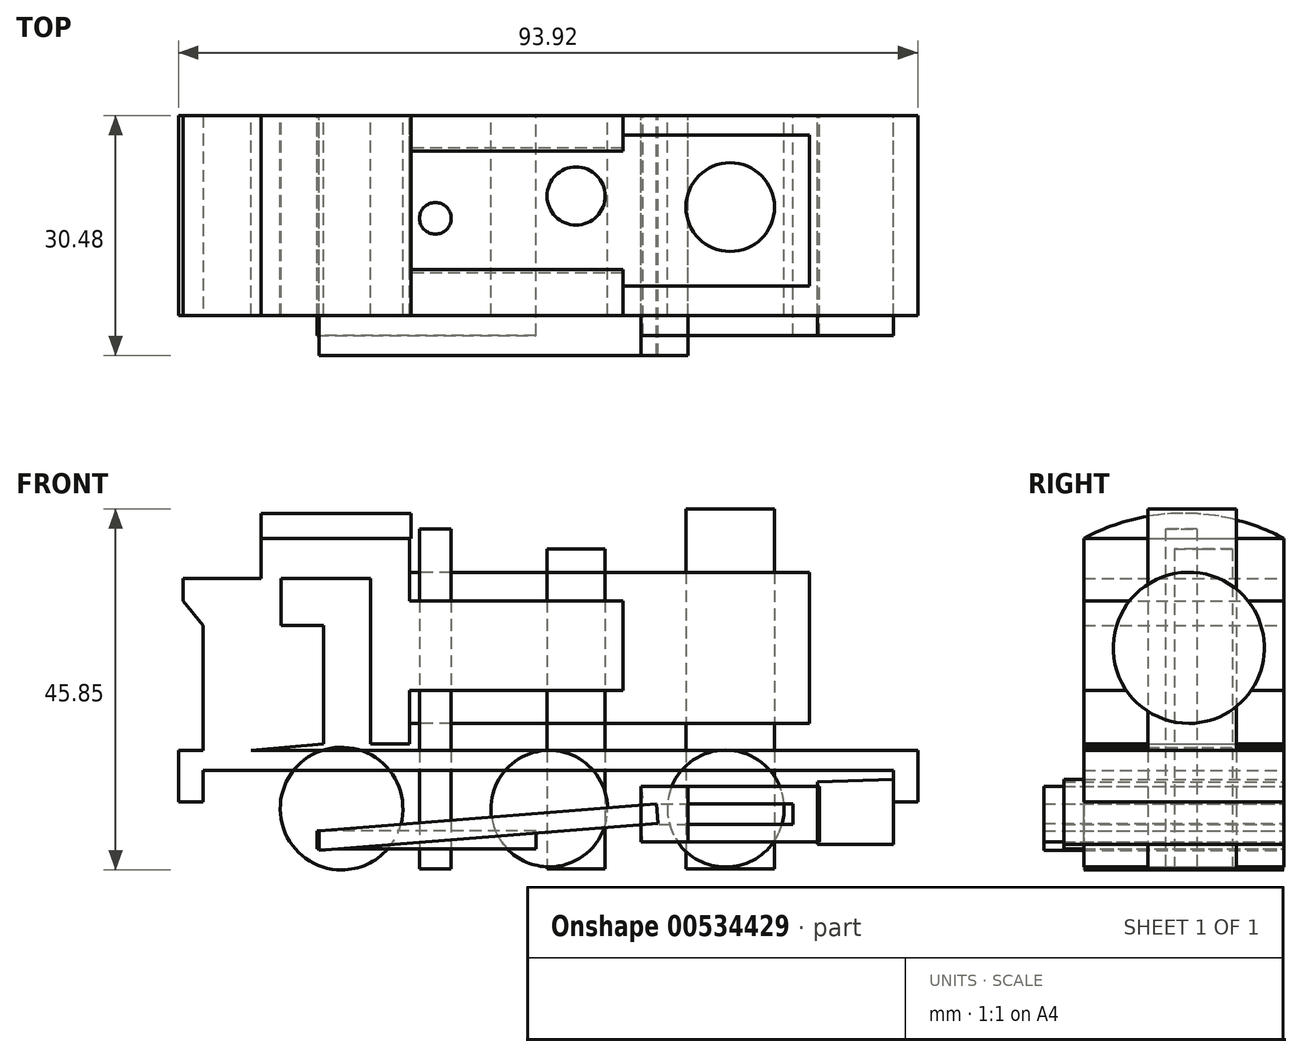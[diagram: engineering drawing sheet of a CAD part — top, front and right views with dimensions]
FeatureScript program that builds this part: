
annotation { "Feature Type Name" : "Feature", "Feature Type Description" : "" }
export const myFeature = defineFeature(function(context is Context, id is Id, definition is map)
    precondition{}
    {
        {
            var Q0;
            Q0=qCreatedBy(makeId("Front.planeOp"),FACE);
            var sketch = newSketch(context, id + "F0", { "sketchPlane" : qUnion([Q0])});
            skCircle(sketch, "E0", {"center": v(-8.65, 7.66) * mm, "radius": 7.8 * mm});
            skCircle(sketch, "E1", {"center": v(17.73, 7.66) * mm, "radius": 7.4 * mm});
            skCircle(sketch, "E2", {"center": v(40.15, 7.66) * mm, "radius": 7.43 * mm});
            skSolve(sketch);
        }
        {
            var Q0;
            Q0=makeQuery(id+"F0.imprint","IMPRINT",FACE,{"disambiguationData":[TD([[makeQuery(id+"F0.imprint","IMPRINT",EDGE,{"derivedFrom":sQuery(id+"F0.wireOp",EDGE,"E0")}),1.0]])]});
            var Q1;
            Q1=makeQuery(id+"F0.imprint","IMPRINT",FACE,{"disambiguationData":[TD([[makeQuery(id+"F0.imprint","IMPRINT",EDGE,{"derivedFrom":sQuery(id+"F0.wireOp",EDGE,"E1")}),1.0]])]});
            var Q2;
            Q2=makeQuery(id+"F0.imprint","IMPRINT",FACE,{"disambiguationData":[TD([[makeQuery(id+"F0.imprint","IMPRINT",EDGE,{"derivedFrom":sQuery(id+"F0.wireOp",EDGE,"E2")}),1.0]])]});
            extrude(context, id + "F1", {"entities" : qUnion([Q0, Q1, Q2]), "depth" : 25.4 * mm, "offsetDistance" : 25.4 * mm});
        }
        {
            var Q0;
            Q0=qCreatedBy(makeId("Front.planeOp"),FACE);
            var sketch = newSketch(context, id + "F2", { "sketchPlane" : qUnion([Q0])});
            skLineSegment(sketch, "E3", {"start": v(-12.06, 15.04) * mm, "end": v(64.55, 15.04) * mm});
            skLineSegment(sketch, "E4", {"start": v(64.55, 15.04) * mm, "end": v(64.55, 8.51) * mm});
            skLineSegment(sketch, "E5", {"start": v(64.55, 8.51) * mm, "end": v(61.43, 8.51) * mm});
            skLineSegment(sketch, "E6", {"start": v(61.43, 8.51) * mm, "end": v(61.43, 12.48) * mm});
            skLineSegment(sketch, "E7", {"start": v(61.43, 12.48) * mm, "end": v(-26.24, 12.48) * mm});
            skLineSegment(sketch, "E8", {"start": v(-26.24, 12.48) * mm, "end": v(-26.24, 8.51) * mm});
            skLineSegment(sketch, "E9", {"start": v(-26.24, 8.51) * mm, "end": v(-29.37, 8.51) * mm});
            skLineSegment(sketch, "E10", {"start": v(-29.37, 8.51) * mm, "end": v(-29.37, 15.04) * mm});
            skLineSegment(sketch, "E11", {"start": v(-29.37, 15.04) * mm, "end": v(-12.06, 15.04) * mm});
            skSolve(sketch);
        }
        {
            var Q0;
            Q0=makeQuery(id+"F2.imprint","IMPRINT",FACE,{"disambiguationData":[TD([[makeQuery(id+"F2.imprint","IMPRINT",EDGE,{"derivedFrom":sQuery(id+"F2.wireOp",EDGE,"E3")}),-1.0]])]});
            extrude(context, id + "F3", {"entities" : qUnion([Q0]), "depth" : 25.4 * mm, "offsetDistance" : 25.4 * mm});
        }
        {
            var Q0;
            Q0=qCreatedBy(makeId("Front.planeOp"),FACE);
            var sketch = newSketch(context, id + "F4", { "sketchPlane" : qUnion([Q0])});
            skLineSegment(sketch, "E12", {"start": v(-26.24, 14.47) * mm, "end": v(-26.24, 30.93) * mm});
            skLineSegment(sketch, "E13", {"start": v(-26.24, 30.93) * mm, "end": v(-28.8, 34.05) * mm});
            skLineSegment(sketch, "E14", {"start": v(-28.8, 34.05) * mm, "end": v(-28.8, 36.88) * mm});
            skLineSegment(sketch, "E15", {"start": v(-28.8, 36.88) * mm, "end": v(-18.87, 36.88) * mm});
            skLineSegment(sketch, "E16", {"start": v(-18.87, 36.88) * mm, "end": v(-18.87, 42) * mm});
            skLineSegment(sketch, "E17", {"start": v(-18.87, 42) * mm, "end": v(0, 42) * mm});
            skLineSegment(sketch, "E18", {"start": v(0, 42) * mm, "end": v(0, 34.05) * mm});
            skLineSegment(sketch, "E19", {"start": v(0, 34.05) * mm, "end": v(27.1, 34.05) * mm});
            skLineSegment(sketch, "E20", {"start": v(27.1, 34.05) * mm, "end": v(27.1, 22.7) * mm});
            skLineSegment(sketch, "E21", {"start": v(27.1, 22.7) * mm, "end": v(0, 22.7) * mm});
            skLineSegment(sketch, "E22", {"start": v(0, 22.7) * mm, "end": v(0, 15.89) * mm});
            skLineSegment(sketch, "E23", {"start": v(0, 15.89) * mm, "end": v(-4.97, 15.89) * mm});
            skLineSegment(sketch, "E24", {"start": v(-4.97, 15.89) * mm, "end": v(-4.97, 36.88) * mm});
            skLineSegment(sketch, "E25", {"start": v(-4.97, 36.88) * mm, "end": v(-16.31, 36.88) * mm});
            skLineSegment(sketch, "E26", {"start": v(-16.31, 36.88) * mm, "end": v(-16.31, 30.93) * mm});
            skLineSegment(sketch, "E27", {"start": v(-16.31, 30.93) * mm, "end": v(-10.92, 30.93) * mm});
            skLineSegment(sketch, "E28", {"start": v(-10.92, 30.93) * mm, "end": v(-10.92, 15.89) * mm});
            skLineSegment(sketch, "E29", {"start": v(-10.92, 15.89) * mm, "end": v(-26.24, 14.47) * mm});
            skSolve(sketch);
        }
        {
            var Q0;
            Q0=makeQuery(id+"F4.imprint","IMPRINT",FACE,{"disambiguationData":[TD([[makeQuery(id+"F4.imprint","IMPRINT",EDGE,{"derivedFrom":sQuery(id+"F4.wireOp",EDGE,"E12")}),-1.0]])]});
            extrude(context, id + "F5", {"entities" : qUnion([Q0]), "operationType" : NewBodyOperationType.ADD, "depth" : 25.4 * mm, "offsetDistance" : 25.4 * mm});
        }
        {
            var Q0;
            Q0=qCreatedBy(makeId("Right.planeOp"),FACE);
            var sketch = newSketch(context, id + "F6", { "sketchPlane" : qUnion([Q0])});
            skCircle(sketch, "E30", {"center": v(-12.06, 28.09) * mm, "radius": 9.6 * mm});
            skSolve(sketch);
        }
        {
            var Q0;
            Q0=makeQuery(id+"F6.imprint","IMPRINT",FACE,{"disambiguationData":[TD([[makeQuery(id+"F6.imprint","IMPRINT",EDGE,{"derivedFrom":sQuery(id+"F6.wireOp",EDGE,"E30")}),1.0]])]});
            var Q1;
            Q1=sQuery(id+"F6.wireOp",EDGE,"E30");
            extrude(context, id + "F7", {"entities" : qUnion([Q0]), "operationType" : NewBodyOperationType.ADD, "surfaceEntities" : qUnion([Q1]), "depth" : 50.8 * mm, "offsetDistance" : 25.4 * mm});
        }
        {
            var Q0;
            Q0=qCreatedBy(makeId("Front.planeOp"),FACE);
            var sketch = newSketch(context, id + "F8", { "sketchPlane" : qUnion([Q0])});
            skLineSegment(sketch, "E31", {"start": v(61.43, 11.35) * mm, "end": v(61.43, 3.12) * mm});
            skLineSegment(sketch, "E32", {"start": v(61.43, 3.12) * mm, "end": v(51.78, 3.12) * mm});
            skLineSegment(sketch, "E33", {"start": v(51.78, 3.12) * mm, "end": v(51.78, 11.07) * mm});
            skLineSegment(sketch, "E34", {"start": v(51.78, 11.07) * mm, "end": v(61.43, 11.35) * mm});
            skSolve(sketch);
        }
        {
            var Q0;
            Q0=makeQuery(id+"F8.imprint","IMPRINT",FACE,{"disambiguationData":[TD([[makeQuery(id+"F8.imprint","IMPRINT",EDGE,{"derivedFrom":sQuery(id+"F8.wireOp",EDGE,"E31")}),-1.0]])]});
            extrude(context, id + "F9", {"entities" : qUnion([Q0]), "operationType" : NewBodyOperationType.ADD, "depth" : 27.94 * mm, "offsetDistance" : 25.4 * mm});
        }
        {
            var Q0;
            Q0=qCreatedBy(makeId("Front.planeOp"),FACE);
            var sketch = newSketch(context, id + "F10", { "sketchPlane" : qUnion([Q0])});
            skLineSegment(sketch, "E35", {"start": v(52.06, 10.5) * mm, "end": v(29.37, 10.5) * mm});
            skLineSegment(sketch, "E36", {"start": v(52.06, 3.4) * mm, "end": v(29.65, 3.4) * mm});
            skLineSegment(sketch, "E37", {"start": v(29.65, 3.4) * mm, "end": v(29.37, 5.67) * mm});
            skLineSegment(sketch, "E38", {"start": v(29.37, 5.67) * mm, "end": v(48.66, 5.67) * mm});
            skLineSegment(sketch, "E39", {"start": v(29.37, 10.5) * mm, "end": v(29.65, 8.23) * mm});
            skLineSegment(sketch, "E40", {"start": v(29.65, 8.23) * mm, "end": v(48.66, 8.23) * mm});
            skLineSegment(sketch, "E41", {"start": v(48.66, 8.23) * mm, "end": v(48.66, 5.67) * mm});
            skLineSegment(sketch, "E42", {"start": v(52.06, 10.5) * mm, "end": v(52.06, 3.4) * mm});
            skLineSegment(sketch, "E43", {"start": v(52.06, 3.4) * mm, "end": v(52.06, 10.5) * mm});
            skSolve(sketch);
        }
        {
            var Q0;
            Q0=makeQuery(id+"F10.imprint","IMPRINT",FACE,{"disambiguationData":[TD([[makeQuery(id+"F10.imprint","IMPRINT",EDGE,{"derivedFrom":sQuery(id+"F10.wireOp",EDGE,"E35")}),1.0]])]});
            extrude(context, id + "F11", {"entities" : qUnion([Q0]), "depth" : 27.94 * mm, "offsetDistance" : 25.4 * mm});
        }
        {
            var Q0;
            Q0=qCreatedBy(makeId("Front.planeOp"),FACE);
            var sketch = newSketch(context, id + "F12", { "sketchPlane" : qUnion([Q0])});
            skLineSegment(sketch, "E44", {"start": v(-11.77, 4.82) * mm, "end": v(-11.77, 2.55) * mm});
            skLineSegment(sketch, "E45", {"start": v(-11.77, 2.55) * mm, "end": v(16.03, 2.55) * mm});
            skLineSegment(sketch, "E46", {"start": v(16.03, 2.55) * mm, "end": v(16.03, 4.82) * mm});
            skLineSegment(sketch, "E47", {"start": v(16.03, 4.82) * mm, "end": v(-11.77, 4.82) * mm});
            skSolve(sketch);
        }
        {
            var Q0;
            Q0=makeQuery(id+"F12.imprint","IMPRINT",FACE,{"disambiguationData":[TD([[makeQuery(id+"F12.imprint","IMPRINT",EDGE,{"derivedFrom":sQuery(id+"F12.wireOp",EDGE,"E44")}),1.0]])]});
            extrude(context, id + "F13", {"entities" : qUnion([Q0]), "depth" : 27.94 * mm, "offsetDistance" : 25.4 * mm});
        }
        {
            var Q0;
            Q0=qCreatedBy(makeId("Front.planeOp"),FACE);
            var sketch = newSketch(context, id + "F14", { "sketchPlane" : qUnion([Q0])});
            skLineSegment(sketch, "E48", {"start": v(29.37, 10.5) * mm, "end": v(35.32, 10.5) * mm});
            skLineSegment(sketch, "E49", {"start": v(35.32, 10.5) * mm, "end": v(35.32, 3.4) * mm});
            skLineSegment(sketch, "E50", {"start": v(35.32, 3.4) * mm, "end": v(29.37, 3.4) * mm});
            skLineSegment(sketch, "E51", {"start": v(29.37, 3.4) * mm, "end": v(29.37, 10.5) * mm});
            skSolve(sketch);
        }
        {
            var Q0;
            Q0=makeQuery(id+"F14.imprint","IMPRINT",FACE,{"disambiguationData":[TD([[makeQuery(id+"F14.imprint","IMPRINT",EDGE,{"derivedFrom":sQuery(id+"F14.wireOp",EDGE,"E48")}),-1.0]])]});
            extrude(context, id + "F15", {"entities" : qUnion([Q0]), "depth" : 30.48 * mm, "offsetDistance" : 25.4 * mm});
        }
        {
            var Q0;
            Q0=qCreatedBy(makeId("Front.planeOp"),FACE);
            var sketch = newSketch(context, id + "F16", { "sketchPlane" : qUnion([Q0])});
            skLineSegment(sketch, "E52", {"start": v(-11.5, 4.82) * mm, "end": v(31.35, 8.23) * mm});
            skLineSegment(sketch, "E53", {"start": v(31.35, 8.23) * mm, "end": v(31.55, 5.78) * mm});
            skLineSegment(sketch, "E54", {"start": v(31.55, 5.78) * mm, "end": v(-11.5, 2.36) * mm});
            skLineSegment(sketch, "E55", {"start": v(-11.5, 2.36) * mm, "end": v(-11.5, 4.82) * mm});
            skLineSegment(sketch, "E56", {"start": v(-11.5, 4.82) * mm, "end": v(-11.5, 2.36) * mm});
            skSolve(sketch);
        }
        {
            var Q0;
            Q0=makeQuery(id+"F16.imprint","IMPRINT",FACE,{"disambiguationData":[TD([[makeQuery(id+"F16.imprint","IMPRINT",EDGE,{"derivedFrom":sQuery(id+"F16.wireOp",EDGE,"E52")}),-1.0]])]});
            extrude(context, id + "F17", {"entities" : qUnion([Q0]), "depth" : 30.48 * mm, "offsetDistance" : 25.4 * mm});
        }
        {
            var Q0;
            Q0=qCreatedBy(makeId("Top.planeOp"),FACE);
            var sketch = newSketch(context, id + "F18", { "sketchPlane" : qUnion([Q0])});
            skCircle(sketch, "E57", {"center": v(40.71, -11.63) * mm, "radius": 5.63 * mm});
            skSolve(sketch);
        }
        {
            var Q0;
            Q0=makeQuery(id+"F18.imprint","IMPRINT",FACE,{"disambiguationData":[TD([[makeQuery(id+"F18.imprint","IMPRINT",EDGE,{"derivedFrom":sQuery(id+"F18.wireOp",EDGE,"E57")}),1.0]])]});
            extrude(context, id + "F19", {"entities" : qUnion([Q0]), "depth" : 45.72 * mm, "offsetDistance" : 25.4 * mm});
        }
        {
            var Q0;
            Q0=qCreatedBy(makeId("Top.planeOp"),FACE);
            var sketch = newSketch(context, id + "F20", { "sketchPlane" : qUnion([Q0])});
            skCircle(sketch, "E58", {"center": v(21.14, -10.21) * mm, "radius": 3.69 * mm});
            skSolve(sketch);
        }
        {
            var Q0;
            Q0=makeQuery(id+"F20.imprint","IMPRINT",FACE,{"disambiguationData":[TD([[makeQuery(id+"F20.imprint","IMPRINT",EDGE,{"derivedFrom":sQuery(id+"F20.wireOp",EDGE,"E58")}),1.0]])]});
            extrude(context, id + "F21", {"entities" : qUnion([Q0]), "depth" : 40.64 * mm, "offsetDistance" : 25.4 * mm});
        }
        {
            var Q0;
            Q0=qCreatedBy(makeId("Top.planeOp"),FACE);
            var sketch = newSketch(context, id + "F22", { "sketchPlane" : qUnion([Q0])});
            skCircle(sketch, "E59", {"center": v(3.26, -13.05) * mm, "radius": 2 * mm});
            skSolve(sketch);
        }
        {
            var Q0;
            Q0=makeQuery(id+"F22.imprint","IMPRINT",FACE,{"disambiguationData":[TD([[makeQuery(id+"F22.imprint","IMPRINT",EDGE,{"derivedFrom":sQuery(id+"F22.wireOp",EDGE,"E59")}),1.0]])]});
            extrude(context, id + "F23", {"entities" : qUnion([Q0]), "depth" : 43.18 * mm, "offsetDistance" : 25.4 * mm});
        }
        {
            var Q0;
            Q0=makeQuery(id+"F5.opExtrude","SWEPT_FACE",FACE,{"disambiguationData":[OSD([sQuery(id+"F4.wireOp",EDGE,"E16")])]});
            var sketch = newSketch(context, id + "F24", { "sketchPlane" : qUnion([Q0])});
            skArc(sketch, "E60", {"start": v(25.4, 42) * mm, "mid": v(12.7, 45.18) * mm, "end": v(0, 42) * mm});
            skLineSegment(sketch, "E61", {"start": v(0, 42) * mm, "end": v(25.4, 42) * mm});
            skSolve(sketch);
        }
        {
            var Q0;
            Q0=makeQuery(id+"F24.imprint","IMPRINT",FACE,{"disambiguationData":[TD([[makeQuery(id+"F24.imprint","IMPRINT",EDGE,{"derivedFrom":sQuery(id+"F24.wireOp",EDGE,"E60")}),1.0]])]});
            extrude(context, id + "F25", {"entities" : qUnion([Q0]), "operationType" : NewBodyOperationType.ADD, "oppositeDirection" : true, "depth" : 19.05 * mm, "offsetDistance" : 25.4 * mm});
        }
    });
